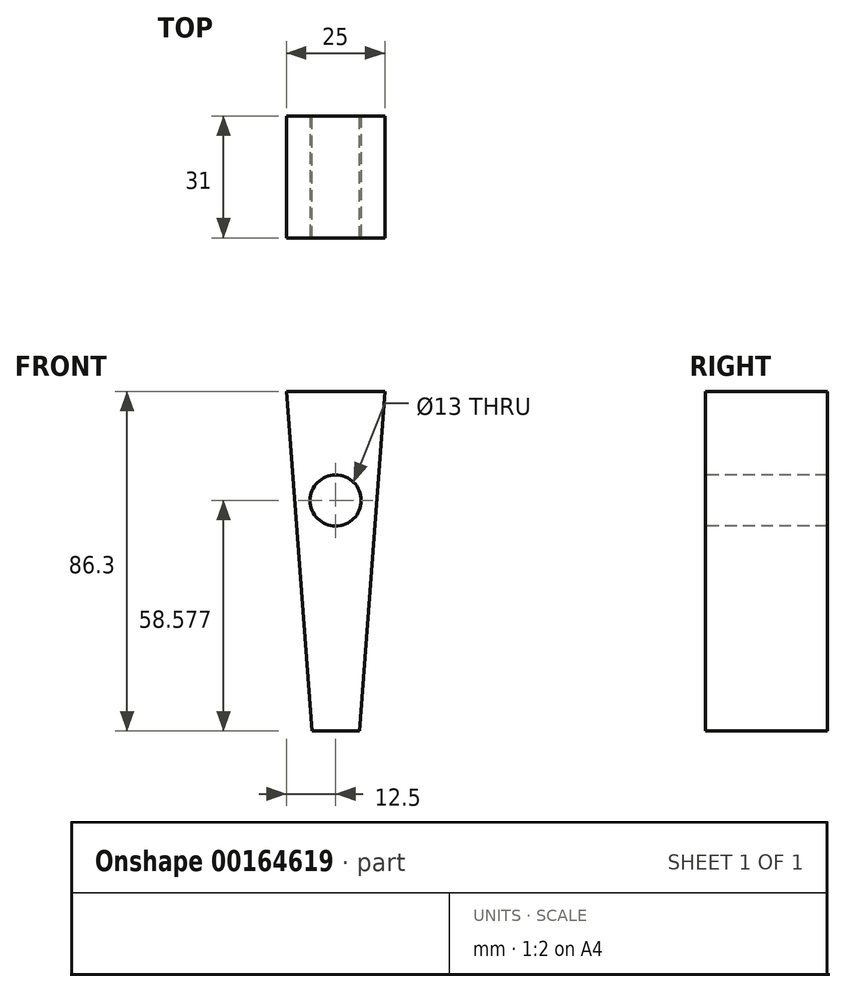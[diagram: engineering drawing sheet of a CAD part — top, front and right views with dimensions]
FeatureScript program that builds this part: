
annotation { "Feature Type Name" : "Feature", "Feature Type Description" : "" }
export const myFeature = defineFeature(function(context is Context, id is Id, definition is map)
    precondition{}
    {
        {
            var Q0;
            Q0=qCreatedBy(makeId("Top.planeOp"),FACE);
            var sketch = newSketch(context, id + "F0", { "sketchPlane" : qUnion([Q0])});
            skLineSegment(sketch, "E0.bottom", {"start": v(-12.5, 15.5) * mm, "end": v(12.5, 15.5) * mm});
            skLineSegment(sketch, "E0.top", {"start": v(-12.5, -15.5) * mm, "end": v(12.5, -15.5) * mm});
            skLineSegment(sketch, "E0.left", {"start": v(-12.5, 15.5) * mm, "end": v(-12.5, -15.5) * mm});
            skLineSegment(sketch, "E0.right", {"start": v(12.5, 15.5) * mm, "end": v(12.5, -15.5) * mm});
            skPoint(sketch, "E0.middle", {"position": v(0, 0) * mm});
            skSolve(sketch);
        }
        {
            var Q0;
            Q0=qSketchRegion(id+"F0",true);
            extrude(context, id + "F1", {"entities" : qUnion([Q0]), "depth" : 86.3 * mm});
        }
        {
            var Q0;
            Q0=qCreatedBy(makeId("Front.planeOp"),FACE);
            var sketch = newSketch(context, id + "F2", { "sketchPlane" : qUnion([Q0])});
            skCircle(sketch, "E1", {"center": v(0, 58.58) * mm, "radius": 6.5 * mm});
            skSolve(sketch);
        }
        {
            var Q0;
            Q0 = qSketchRegion(id + "F2", true);
            extrude(context, id + "F3", {"entities" : qUnion([Q0]), "operationType" : NewBodyOperationType.REMOVE, "endBound" : BoundingType.SYMMETRIC, "oppositeDirection" : true, "depth" : 63 * mm});
        }
        {
            var Q0;
            Q0=makeQuery(id+"F1.opExtrude","SWEPT_FACE",FACE,{"disambiguationData":[OSD([sQuery(id+"F0.wireOp",EDGE,"E0.bottom")])]});
            var sketch = newSketch(context, id + "F4", { "sketchPlane" : qUnion([Q0])});
            skLineSegment(sketch, "E2", {"start": v(-12.5, 86.3) * mm, "end": v(-6, 0) * mm});
            skLineSegment(sketch, "E3", {"start": v(-6, 0) * mm, "end": v(6, 0) * mm});
            skLineSegment(sketch, "E4", {"start": v(6, 0) * mm, "end": v(12.5, 86.3) * mm});
            skSolve(sketch);
        }
        {
            var Q0;
            {var subQ0=sQuery(id+"F4.wireOp",EDGE,"E4");Q0=makeQuery(id+"F4.imprint","IMPRINT",FACE,{"disambiguationData":[TD([[makeQuery(id+"F4.imprint","IMPRINT",EDGE,{"derivedFrom":subQ0}),-1.0]])]});}
            var Q1;
            {var subQ0=sQuery(id+"F4.wireOp",EDGE,"E2");Q1=makeQuery(id+"F4.imprint","IMPRINT",FACE,{"disambiguationData":[TD([[makeQuery(id+"F4.imprint","IMPRINT",EDGE,{"derivedFrom":subQ0}),-1.0]])]});}
            extrude(context, id + "F5", {"entities" : qUnion([Q0, Q1]), "operationType" : NewBodyOperationType.REMOVE, "endBound" : BoundingType.THROUGH_ALL, "oppositeDirection" : true, "depth" : 25 * mm});
        }
    });
